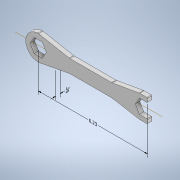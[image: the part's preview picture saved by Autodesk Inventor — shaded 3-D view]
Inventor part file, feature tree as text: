
AUTODESK INVENTOR PART (.ipt)
format: ipt  version: 2020.3 (Build 243373000, 373)  size: 183,296 bytes
history: native  units: in
note: dims shown in document units (in); Inventor stores cm internally (conversion verified against a paired STEP export)
features: other x3, fillet x2, extrude x1, sketch x1
ambient origin geometry x8: Origin, YZ Plane, XZ Plane, XY Plane, X Axis, Y Axis, Z Axis, Center Point
bodies: Body1 (feature_tree)
feature tree (7):
  other  "Annotations"
  extrude  "Extrusion2"  Depth=0.25in
  fillet  "Fillet1"  Radius=0.25in
  fillet  "Fillet2"  Radius=0.25in
  sketch  "Sketch2"  dims[d23=0.375in d24=0.25in d26=0.25in d27=0.25in d28=0.0in d29=0.0312in d30=0.25in d33=0.0967in d34=0.2112in d35=0.25in d36=6.2309in]
  other  "Linear Dimension 1"
  other  "Linear Dimension 2"
